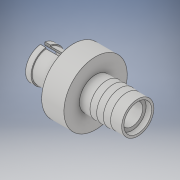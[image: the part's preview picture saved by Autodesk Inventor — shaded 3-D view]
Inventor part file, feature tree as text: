
AUTODESK INVENTOR PART (.ipt)
format: ipt  version: 2018 (Build 220112000, 112)  size: 193,536 bytes
history: native  units: in
note: dims shown in document units (in); Inventor stores cm internally (conversion verified against a paired STEP export)
features: sketch x2, revolve x1, extrude x1
ambient origin geometry x8: Origin, YZ Plane, XZ Plane, XY Plane, X Axis, Y Axis, Z Axis, Center Point
bodies: Solid1 (feature_tree)
feature tree (4):
  revolve  "Revolution1"  [1 undecoded]
  extrude  "Extrusion1"  Depth=0.45in
  sketch  "Sketch1"  dims[d0=0.86in d1=0.05in]
  sketch  "Sketch2"  dims[d2=0.25in d3=0.45in d4=0.2in d5=0.06in d6=0.06in d7=0.06in d8=0.05in d9=0.1in d10=0.1in d11=0.19in d13=0.23in d14=0.285in d15=0.01in d16=0.005in d17=0.005in d18=0.095in d19=0.125in d20=0.145in d21=0.15in d22=0.125in d23=0.095in d24=90.0deg d25=0.04in d26=0.2in d27=0.0in]
note: 1 required parameter value undecoded (feature->parameter linkage not recoverable at this tier; creation-order binding heuristic only, values carry confidence <= 0.55)
